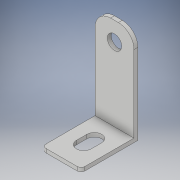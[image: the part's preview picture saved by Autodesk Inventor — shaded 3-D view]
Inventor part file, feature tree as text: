
AUTODESK INVENTOR PART (.ipt)
format: ipt  version: 2018 (Build 220112000, 112)  size: 147,968 bytes
history: native  units: in
note: dims shown in document units (in); Inventor stores cm internally (conversion verified against a paired STEP export)
features: extrude x4, sketch x4, fillet x2
ambient origin geometry x8: Origin, YZ Plane, XZ Plane, XY Plane, X Axis, Y Axis, Z Axis, Center Point
bodies: Solid1 (feature_tree)
feature tree (10):
  extrude  "Extrusion1"  Depth=0.5748in
  extrude  "Extrusion2"  Depth=0.9724in
  fillet  "Fillet1"  Radius=0.0394in
  fillet  "Fillet2"  Radius=0.1575in
  extrude  "Extrusion3"  Depth=0.0394in
  extrude  "Extrusion4"  Depth=0.0394in
  sketch  "Sketch1"  dims[d0=0.3937in d1=0.5748in]
  sketch  "Sketch2"  dims[d2=0.0394in d3=0.0in d4=0.9724in d5=0.0394in d6=0.0in d7=0.1575in]
  sketch  "Sketch3"  dims[d8=0.0394in d9=0.1457in]
  sketch  "Sketch4"  dims[d10=0.1969in d11=0.1181in d12=0.0394in d13=0.0in d14=0.1496in d15=0.1969in d17=0.1496in d18=0.1496in d19=0.2559in d20=0.1969in d21=0.0394in d22=0.0in]
